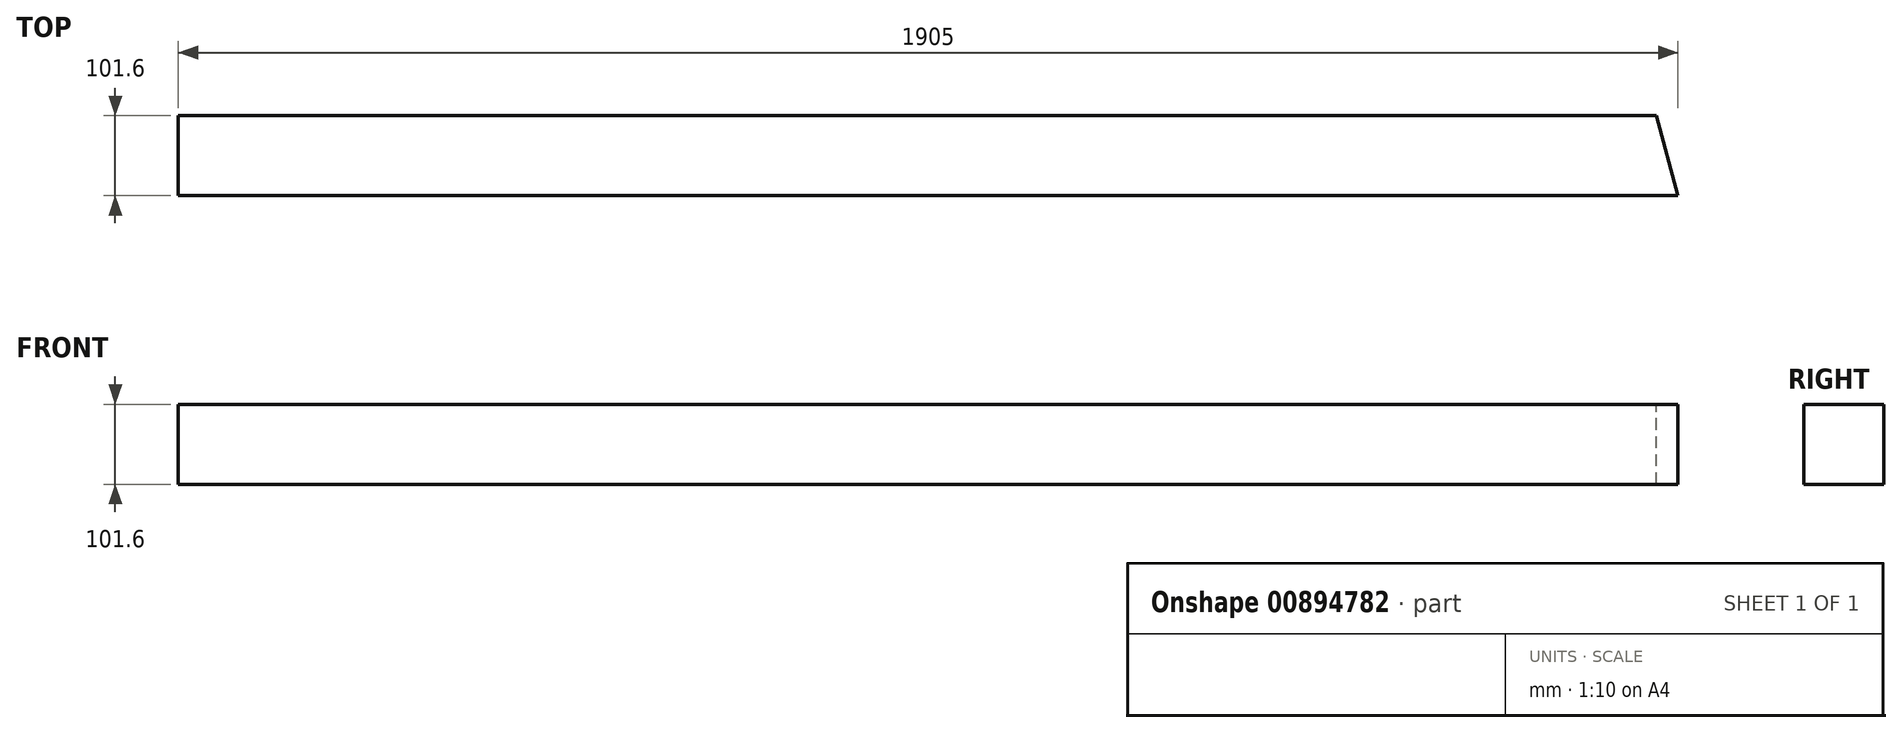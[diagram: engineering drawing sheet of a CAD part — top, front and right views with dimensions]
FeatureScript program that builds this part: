
annotation { "Feature Type Name" : "Feature", "Feature Type Description" : "" }
export const myFeature = defineFeature(function(context is Context, id is Id, definition is map)
    precondition{}
    {
        {
            var Q0;
            Q0=qCreatedBy(makeId("Right.planeOp"),FACE);
            var sketch = newSketch(context, id + "F0", { "sketchPlane" : qUnion([Q0])});
            skLineSegment(sketch, "E0.bottom", {"start": v(0, 0) * mm, "end": v(101.6, 0) * mm});
            skLineSegment(sketch, "E0.top", {"start": v(0, -101.6) * mm, "end": v(101.6, -101.6) * mm});
            skLineSegment(sketch, "E0.left", {"start": v(0, 0) * mm, "end": v(0, -101.6) * mm});
            skLineSegment(sketch, "E0.right", {"start": v(101.6, 0) * mm, "end": v(101.6, -101.6) * mm});
            skSolve(sketch);
        }
        {
            var Q0;
            Q0=qSketchRegion(id+"F0",true);
            extrude(context, id + "F1", {"entities" : qUnion([Q0]), "depth" : 1905 * mm, "offsetDistance" : 25.4 * mm});
        }
        {
            var Q0;
            Q0=qCreatedBy(makeId("Top.planeOp"),FACE);
            var sketch = newSketch(context, id + "F2", { "sketchPlane" : qUnion([Q0])});
            skLineSegment(sketch, "E1", {"start": v(1877.78, 101.6) * mm, "end": v(1905, 0) * mm});
            skLineSegment(sketch, "E2", {"start": v(1877.78, 101.6) * mm, "end": v(1905, 101.6) * mm});
            skLineSegment(sketch, "E3", {"start": v(1905, 101.6) * mm, "end": v(1905, 0) * mm});
            skSolve(sketch);
        }
        {
            var Q0;
            Q0 = qSketchRegion(id + "F2", true);
            extrude(context, id + "F3", {"entities" : qUnion([Q0]), "operationType" : NewBodyOperationType.REMOVE, "oppositeDirection" : true, "depth" : 127 * mm, "offsetDistance" : 25.4 * mm});
        }
    });
